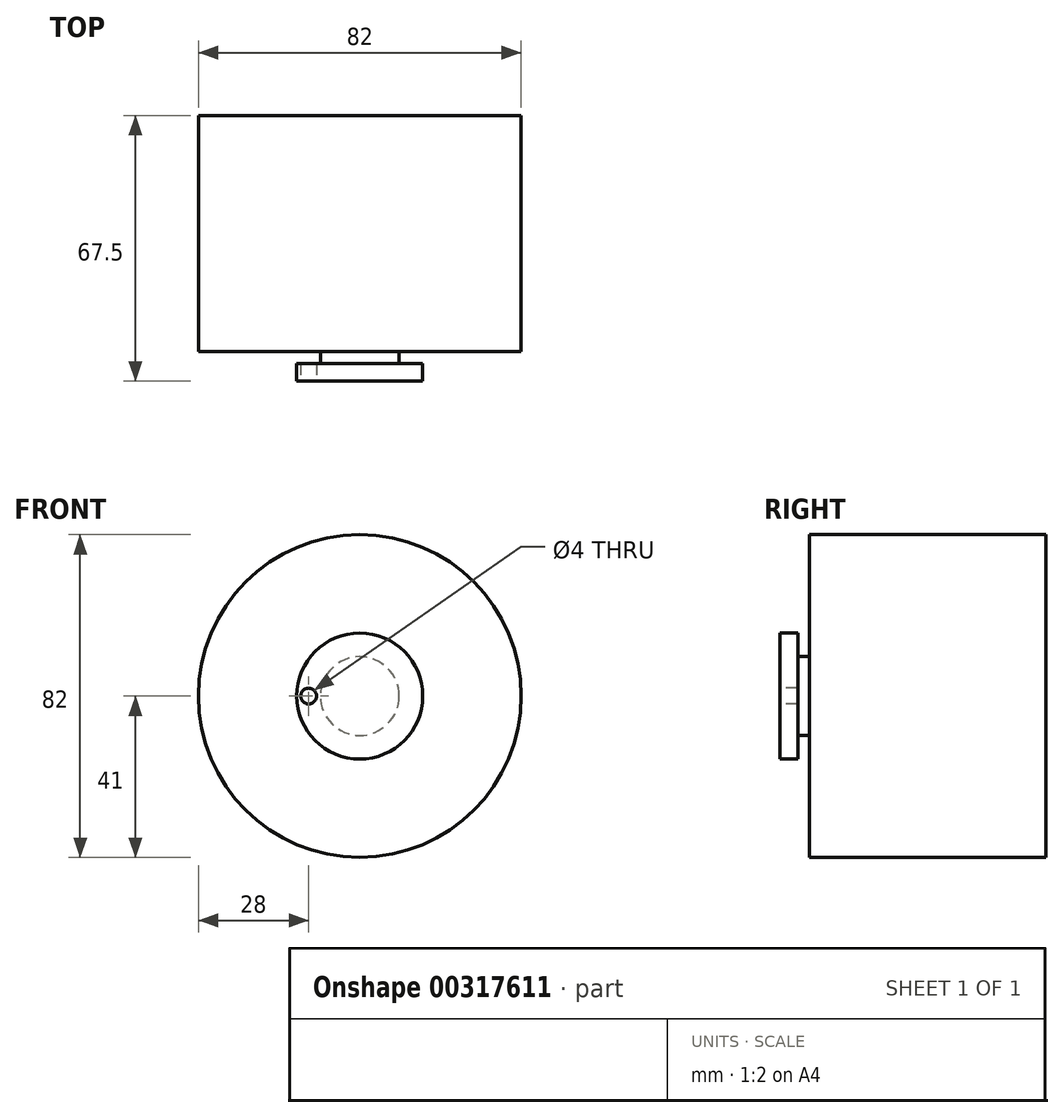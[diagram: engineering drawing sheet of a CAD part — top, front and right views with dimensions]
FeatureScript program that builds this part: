
annotation { "Feature Type Name" : "Feature", "Feature Type Description" : "" }
export const myFeature = defineFeature(function(context is Context, id is Id, definition is map)
    precondition{}
    {
        {
            var Q0;
            Q0=qCreatedBy(makeId("Front.planeOp"),FACE);
            var sketch = newSketch(context, id + "F0", { "sketchPlane" : qUnion([Q0])});
            skCircle(sketch, "E0", {"center": v(0, 0) * mm, "radius": 41 * mm});
            skSolve(sketch);
        }
        {
            var Q0;
            Q0=makeQuery(id+"F0.imprint","IMPRINT",FACE,{"disambiguationData":[TD([[makeQuery(id+"F0.imprint","IMPRINT",EDGE,{"derivedFrom":sQuery(id+"F0.wireOp",EDGE,"E0")}),1.0]])]});
            extrude(context, id + "F1", {"entities" : qUnion([Q0]), "depth" : 30 * mm, "hasSecondDirection" : true, "secondDirectionOppositeDirection" : true, "secondDirectionDepth" : 30 * mm});
        }
        {
            var Q0;
            Q0=makeQuery(id+"F1.opExtrude","CAP_FACE",FACE,{"disambiguationData":[OSD([sQuery(id+"F0.wireOp",EDGE,"E0")])],"isStart":false});
            var sketch = newSketch(context, id + "F2", { "sketchPlane" : qUnion([Q0])});
            skCircle(sketch, "E1", {"center": v(0, 0) * mm, "radius": 10 * mm});
            skSolve(sketch);
        }
        {
            var Q0;
            Q0=makeQuery(id+"F2.imprint","IMPRINT",FACE,{"disambiguationData":[TD([[makeQuery(id+"F2.imprint","IMPRINT",EDGE,{"derivedFrom":sQuery(id+"F2.wireOp",EDGE,"E1")}),1.0]])]});
            extrude(context, id + "F3", {"entities" : qUnion([Q0]), "operationType" : NewBodyOperationType.ADD, "depth" : 3 * mm});
        }
        {
            var Q0;
            Q0=makeQuery(id+"F3.opExtrude","CAP_FACE",FACE,{"disambiguationData":[OSD([sQuery(id+"F2.wireOp",EDGE,"E1")])],"isStart":false});
            var sketch = newSketch(context, id + "F4", { "sketchPlane" : qUnion([Q0])});
            skCircle(sketch, "E2", {"center": v(0, 0) * mm, "radius": 16 * mm});
            skSolve(sketch);
        }
        {
            var Q0;
            Q0 = qSketchRegion(id + "F4", true);
            extrude(context, id + "F5", {"entities" : qUnion([Q0]), "operationType" : NewBodyOperationType.ADD, "depth" : 4.5 * mm});
        }
        {
            var Q0;
            Q0=makeQuery(id+"F5.opExtrude","CAP_FACE",FACE,{"disambiguationData":[OSD([sQuery(id+"F4.wireOp",EDGE,"E2")])],"isStart":false});
            var sketch = newSketch(context, id + "F6", { "sketchPlane" : qUnion([Q0])});
            skPoint(sketch, "E3", {"position": v(-13, 0) * mm});
            skSolve(sketch);
        }
        {
            var Q0;
            Q0=sQuery(id+"F6.wireOp",VERTEX,"E3");
            var Q1;
            Q1=makeQuery(id+"F1.opExtrude","SWEPT_BODY",BODY,{"disambiguationData":[OSD([sQuery(id+"F0.wireOp",EDGE,"E0")])]});
            hole(context, id + "F7", {"style" : HoleStyle.SIMPLE, "endStyle" : HoleEndStyle.BLIND, "holeDiameter" : 4 * mm, "holeDepth" : 5 * mm, "tappedDepth" : 12 * mm, "tapClearance" : 3, "startFromSketch" : true, "locations" : qUnion([Q0]), "scope" : qUnion([Q1])});
        }
    });
